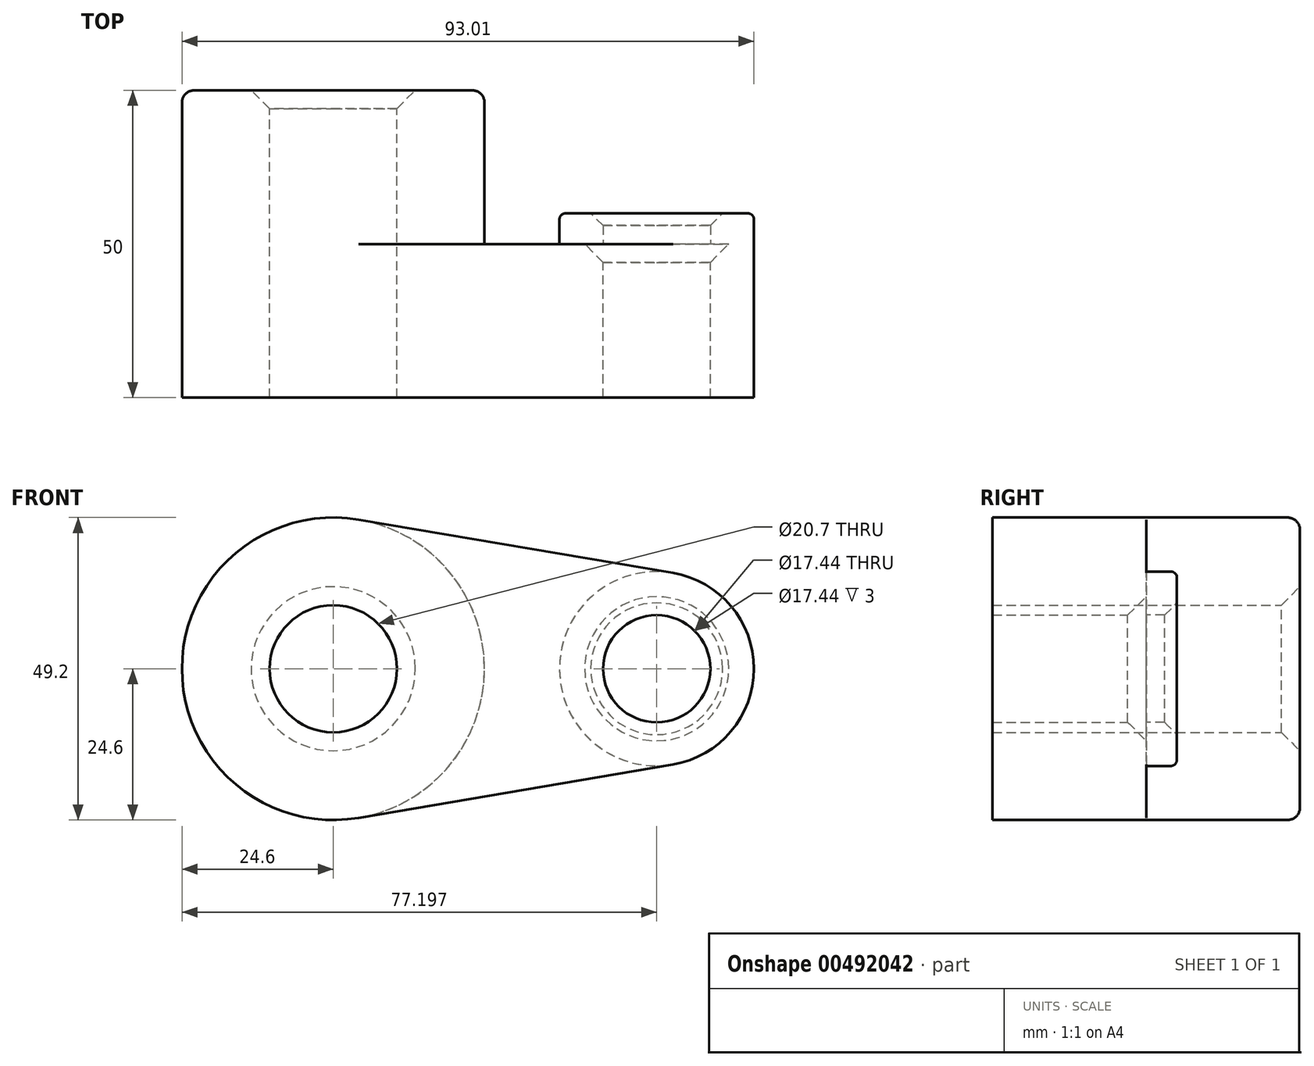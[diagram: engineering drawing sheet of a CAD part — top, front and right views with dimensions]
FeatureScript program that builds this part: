
annotation { "Feature Type Name" : "Feature", "Feature Type Description" : "" }
export const myFeature = defineFeature(function(context is Context, id is Id, definition is map)
    precondition{}
    {
        {
            var Q0;
            Q0=qCreatedBy(makeId("Front.planeOp"),FACE);
            var sketch = newSketch(context, id + "F0", { "sketchPlane" : qUnion([Q0])});
            skCircle(sketch, "E0", {"center": v(0, 0) * mm, "radius": 24.6 * mm});
            skCircle(sketch, "E1", {"center": v(52.6, 0) * mm, "radius": 15.8 * mm});
            skLineSegment(sketch, "E2", {"start": v(4.1, -24.25) * mm, "end": v(55.24, -15.59) * mm});
            skLineSegment(sketch, "E3", {"start": v(4.1, 24.25) * mm, "end": v(55.24, 15.59) * mm});
            skCircle(sketch, "E4", {"center": v(0, 0) * mm, "radius": 10.35 * mm});
            skCircle(sketch, "E5", {"center": v(52.6, 0) * mm, "radius": 8.72 * mm});
            skSolve(sketch);
        }
        {
            var Q0;
            Q0 = qSketchRegion(id + "F0", true);
            extrude(context, id + "F1", {"entities" : qUnion([Q0]), "depth" : 25 * mm});
        }
        {
            var Q0;
            Q0=makeQuery(id+"F0.imprint","IMPRINT",FACE,{"disambiguationData":[TD([[makeQuery(id+"F0.imprint","IMPRINT",EDGE,{"derivedFrom":sQuery(id+"F0.wireOp",EDGE,"E4")}),-1.0]])]});
            extrude(context, id + "F2", {"entities" : qUnion([Q0]), "operationType" : NewBodyOperationType.ADD, "oppositeDirection" : true, "depth" : 25 * mm});
        }
        {
            var Q0;
            Q0=makeQuery(id+"F2.opExtrude","CAP_EDGE",EDGE,{"disambiguationData":[OSD([sQuery(id+"F0.wireOp",EDGE,"E4")])],"isStart":false});
            var Q1;
            Q1=makeQuery(id+"F1.opExtrude","CAP_EDGE",EDGE,{"disambiguationData":[OSD([sQuery(id+"F0.wireOp",EDGE,"E5")])],"isStart":true});
            chamfer(context, id + "F3", {"entities" : qUnion([Q0, Q1]), "width" : 3 * mm, "tangentPropagation" : true});
        }
        {
            var Q0;
            Q0=makeQuery(id+"F2.opExtrude","CAP_EDGE",EDGE,{"disambiguationData":[OSD([sQuery(id+"F0.wireOp",EDGE,"E0")])],"isStart":false});
            fillet(context, id + "F4", {"entities" : qUnion([Q0]), "radius" : 2 * mm, "tangentPropagation" : true, "allowEdgeOverflow" : false});
        }
        {
            var Q0;
            Q0=makeQuery(id+"F0.imprint","IMPRINT",FACE,{"disambiguationData":[TD([[makeQuery(id+"F0.imprint","IMPRINT",EDGE,{"derivedFrom":sQuery(id+"F0.wireOp",EDGE,"E5")}),-1.0]])]});
            extrude(context, id + "F5", {"entities" : qUnion([Q0]), "operationType" : NewBodyOperationType.ADD, "oppositeDirection" : true, "depth" : 5 * mm, "offsetDistance" : 25 * mm});
        }
        {
            var Q0;
            Q0=makeQuery(id+"F5.opExtrude","CAP_EDGE",EDGE,{"disambiguationData":[OSD([sQuery(id+"F0.wireOp",EDGE,"E1")])],"isStart":false});
            fillet(context, id + "F6", {"entities" : qUnion([Q0]), "radius" : 1 * mm, "tangentPropagation" : true, "allowEdgeOverflow" : false});
        }
        {
            var Q0;
            Q0=makeQuery(id+"F5.opExtrude","CAP_EDGE",EDGE,{"disambiguationData":[OSD([sQuery(id+"F0.wireOp",EDGE,"E5")])],"isStart":false});
            chamfer(context, id + "F7", {"entities" : qUnion([Q0]), "width" : 2 * mm, "tangentPropagation" : true});
        }
    });
